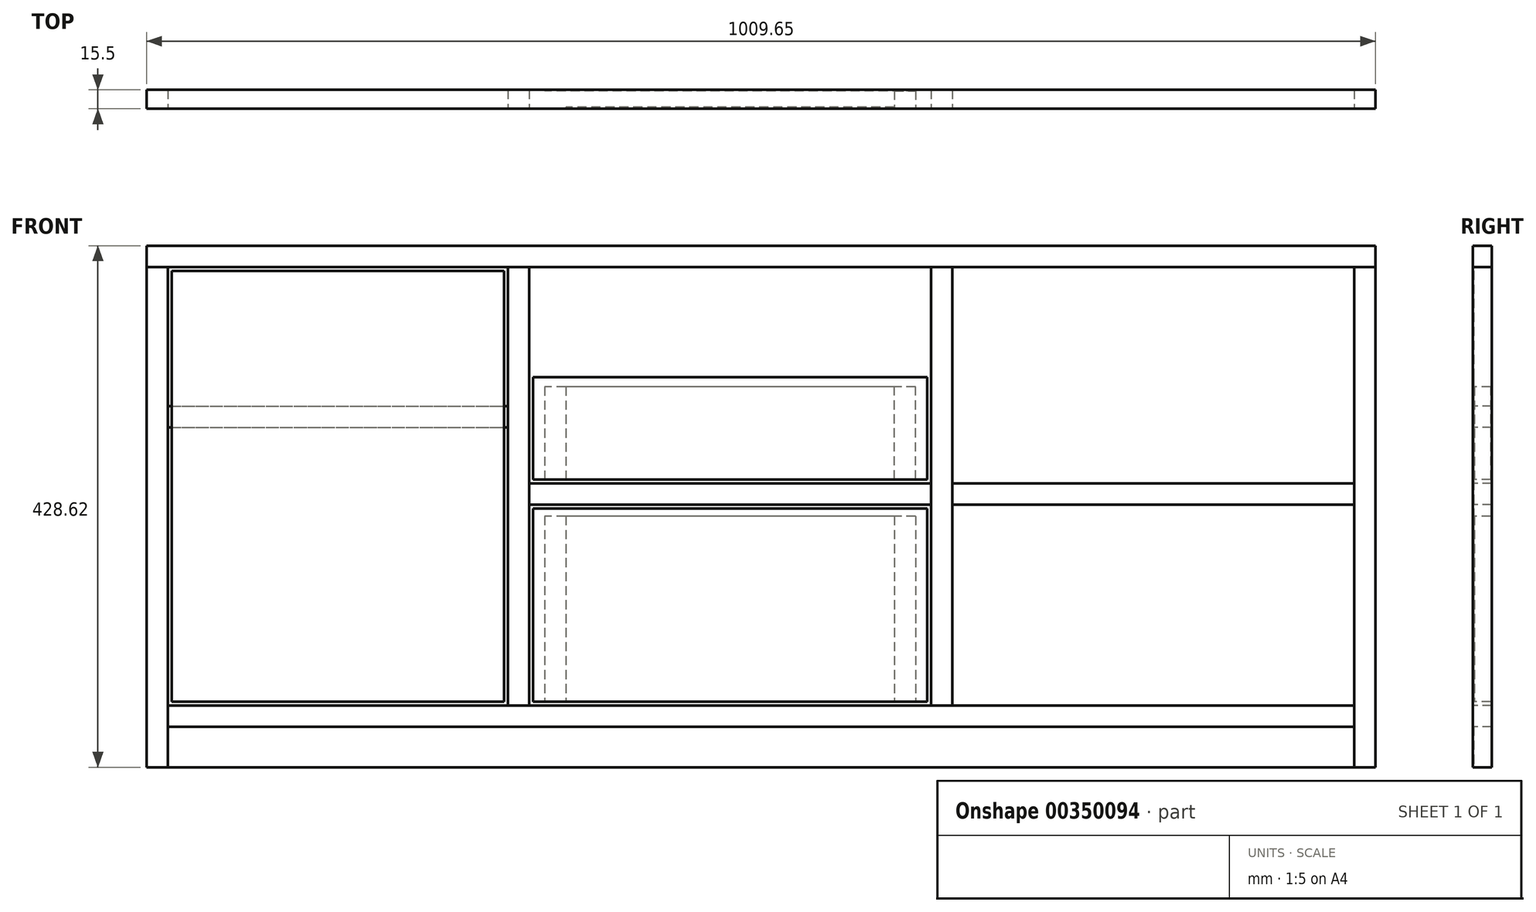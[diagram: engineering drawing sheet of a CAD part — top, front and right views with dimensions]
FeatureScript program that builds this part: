
annotation { "Feature Type Name" : "Feature", "Feature Type Description" : "" }
export const myFeature = defineFeature(function(context is Context, id is Id, definition is map)
    precondition{}
    {
        {
            assignVariable(context, id + "F0", {"name" : "Thk", "anyValue" : .6875});
        }
        {
            assignVariable(context, id + "F1", {"name" : "Depth", "anyValue" : 15.5});
        }
        {
            var Q0;
            Q0=qCreatedBy(makeId("Front.planeOp"),FACE);
            var sketch = newSketch(context, id + "F2", { "sketchPlane" : qUnion([Q0])});
            skLineSegment(sketch, "E0.bottom", {"start": v(0, 0) * mm, "end": v(1009.65, 0) * mm});
            skLineSegment(sketch, "E0.top", {"start": v(0, 428.62) * mm, "end": v(1009.65, 428.63) * mm});
            skLineSegment(sketch, "E0.left", {"start": v(0, 0) * mm, "end": v(0, 428.62) * mm});
            skLineSegment(sketch, "E0.right", {"start": v(1009.65, 0) * mm, "end": v(1009.65, 428.63) * mm});
            skLineSegment(sketch, "E1", {"start": v(17.46, 50.8) * mm, "end": v(992.19, 50.8) * mm});
            skLineSegment(sketch, "E2", {"start": v(17.46, 50.8) * mm, "end": v(17.46, 411.16) * mm});
            skLineSegment(sketch, "E3", {"start": v(17.46, 411.16) * mm, "end": v(992.19, 411.16) * mm});
            skLineSegment(sketch, "E4", {"start": v(992.19, 411.16) * mm, "end": v(992.19, 50.8) * mm});
            skLineSegment(sketch, "E5", {"start": v(314.33, 215.9) * mm, "end": v(314.32, 411.16) * mm});
            skLineSegment(sketch, "E6", {"start": v(314.33, 215.9) * mm, "end": v(314.33, 50.8) * mm});
            skLineSegment(sketch, "E7", {"start": v(17.46, 279.4) * mm, "end": v(296.86, 279.4) * mm});
            skLineSegment(sketch, "E8", {"start": v(296.86, 279.4) * mm, "end": v(296.86, 50.8) * mm});
            skLineSegment(sketch, "E9", {"start": v(17.46, 296.86) * mm, "end": v(296.86, 296.86) * mm});
            skLineSegment(sketch, "E10", {"start": v(296.86, 296.86) * mm, "end": v(296.86, 411.16) * mm});
            skLineSegment(sketch, "E11", {"start": v(314.32, 215.9) * mm, "end": v(644.52, 215.9) * mm});
            skLineSegment(sketch, "E12", {"start": v(314.32, 233.36) * mm, "end": v(644.52, 233.36) * mm});
            skLineSegment(sketch, "E13", {"start": v(653.26, 215.9) * mm, "end": v(653.26, 50.8) * mm, "construction": true});
            skLineSegment(sketch, "E14", {"start": v(661.99, 215.9) * mm, "end": v(661.99, 50.8) * mm});
            skLineSegment(sketch, "E15.MirrorCS", {"start": v(644.52, 215.9) * mm, "end": v(644.52, 50.8) * mm});
            skLineSegment(sketch, "E16", {"start": v(644.52, 233.36) * mm, "end": v(644.52, 411.16) * mm});
            skLineSegment(sketch, "E17", {"start": v(661.99, 233.36) * mm, "end": v(661.99, 411.16) * mm});
            skPoint(sketch, "E18.startSnap0", {"position": v(661.99, 322.26) * mm});
            skLineSegment(sketch, "E19", {"start": v(661.99, 322.26) * mm, "end": v(992.19, 322.26) * mm});
            skLineSegment(sketch, "E20", {"start": v(644.52, 322.26) * mm, "end": v(314.32, 322.26) * mm});
            skLineSegment(sketch, "E21", {"start": v(17.46, 411.16) * mm, "end": v(0, 411.16) * mm});
            skLineSegment(sketch, "E22", {"start": v(992.19, 411.16) * mm, "end": v(1009.65, 411.16) * mm});
            skLineSegment(sketch, "E23", {"start": v(17.46, 50.8) * mm, "end": v(17.46, 0) * mm});
            skLineSegment(sketch, "E24", {"start": v(17.46, 33.34) * mm, "end": v(992.19, 33.34) * mm});
            skLineSegment(sketch, "E25", {"start": v(992.19, 50.8) * mm, "end": v(992.19, 0) * mm});
            skLineSegment(sketch, "E26", {"start": v(296.86, 296.86) * mm, "end": v(296.86, 279.4) * mm});
            skLineSegment(sketch, "E27", {"start": v(644.52, 233.36) * mm, "end": v(644.52, 215.9) * mm});
            skLineSegment(sketch, "E28", {"start": v(661.99, 233.36) * mm, "end": v(661.99, 215.9) * mm});
            skLineSegment(sketch, "E29.trimOffspring", {"start": v(661.99, 233.36) * mm, "end": v(992.19, 233.36) * mm});
            skLineSegment(sketch, "E30.trimOffspring", {"start": v(661.99, 215.9) * mm, "end": v(992.19, 215.9) * mm});
            skSolve(sketch);
        }
        {
            var Q0;
            {var subQ4=sQuery(id+"F2.wireOp",EDGE,"E0.top");Q0=makeQuery(id+"F2.imprint","IMPRINT",FACE,{"disambiguationData":[TD([[makeQuery(id+"F2.imprint","IMPRINT",EDGE,{"derivedFrom":subQ4}),-1.0]])]});}
            extrude(context, id + "F3", {"entities" : qUnion([Q0]), "oppositeDirection" : true, "depth" : (getVariable(context, 'Depth')) * mm});
        }
        {
            var Q0;
            {var subQ10=sQuery(id+"F2.wireOp",EDGE,"E21");Q0=makeQuery(id+"F2.imprint","IMPRINT",FACE,{"disambiguationData":[TD([[makeQuery(id+"F2.imprint","IMPRINT",EDGE,{"derivedFrom":subQ10}),1.0]])]});}
            extrude(context, id + "F4", {"entities" : qUnion([Q0]), "oppositeDirection" : true, "depth" : (getVariable(context, 'Depth')) * mm});
        }
        {
            var Q0;
            {var subQ3=sQuery(id+"F2.wireOp",EDGE,"E6");Q0=makeQuery(id+"F2.imprint","IMPRINT",FACE,{"disambiguationData":[TD([[makeQuery(id+"F2.imprint","IMPRINT",EDGE,{"derivedFrom":subQ3}),-1.0]])]});}
            extrude(context, id + "F5", {"entities" : qUnion([Q0]), "oppositeDirection" : true, "depth" : (getVariable(context, 'Depth')) * mm});
        }
        {
            var Q0;
            {var subQ0=sQuery(id+"F2.wireOp",EDGE,"E14");Q0=makeQuery(id+"F2.imprint","IMPRINT",FACE,{"disambiguationData":[TD([[makeQuery(id+"F2.imprint","IMPRINT",EDGE,{"derivedFrom":subQ0}),-1.0]])]});}
            extrude(context, id + "F6", {"entities" : qUnion([Q0]), "oppositeDirection" : true, "depth" : (getVariable(context, 'Depth')) * mm});
        }
        {
            var Q0;
            {var subQ0=sQuery(id+"F2.wireOp",EDGE,"E22");Q0=makeQuery(id+"F2.imprint","IMPRINT",FACE,{"disambiguationData":[TD([[makeQuery(id+"F2.imprint","IMPRINT",EDGE,{"derivedFrom":subQ0}),-1.0]])]});}
            extrude(context, id + "F7", {"entities" : qUnion([Q0]), "oppositeDirection" : true, "depth" : (getVariable(context, 'Depth')) * mm});
        }
        {
            var Q0;
            {var subQ0=sQuery(id+"F2.wireOp",EDGE,"E7");Q0=makeQuery(id+"F2.imprint","IMPRINT",FACE,{"disambiguationData":[TD([[makeQuery(id+"F2.imprint","IMPRINT",EDGE,{"derivedFrom":subQ0}),1.0]])]});}
            extrude(context, id + "F8", {"entities" : qUnion([Q0]), "oppositeDirection" : true, "depth" : (getVariable(context, 'Depth')) * mm, "hasSecondDirection" : true, "secondDirectionOppositeDirection" : true, "secondDirectionDepth" : (getVariable(context, 'Thk')) * mm});
        }
        {
            var Q0;
            {var subQ9=sQuery(id+"F2.wireOp",EDGE,"E24");Q0=makeQuery(id+"F2.imprint","IMPRINT",FACE,{"disambiguationData":[TD([[makeQuery(id+"F2.imprint","IMPRINT",EDGE,{"derivedFrom":subQ9}),1.0]])]});}
            extrude(context, id + "F9", {"entities" : qUnion([Q0]), "oppositeDirection" : true, "depth" : (getVariable(context, 'Depth')) * mm});
        }
        {
            var Q0;
            {var subQ5=sQuery(id+"F2.wireOp",EDGE,"E24");Q0=makeQuery(id+"F2.imprint","IMPRINT",FACE,{"disambiguationData":[TD([[makeQuery(id+"F2.imprint","IMPRINT",EDGE,{"derivedFrom":subQ5}),-1.0]])]});}
            extrude(context, id + "F10", {"entities" : qUnion([Q0]), "oppositeDirection" : true, "depth" : (getVariable(context, 'Thk')) * mm});
        }
        {
            var Q0;
            {var subQ0=sQuery(id+"F2.wireOp",EDGE,"E11");Q0=makeQuery(id+"F2.imprint","IMPRINT",FACE,{"disambiguationData":[TD([[makeQuery(id+"F2.imprint","IMPRINT",EDGE,{"derivedFrom":subQ0}),1.0]])]});}
            extrude(context, id + "F11", {"entities" : qUnion([Q0]), "oppositeDirection" : true, "depth" : (getVariable(context, 'Depth')) * mm});
        }
        {
            var Q0;
            Q0=makeQuery(id+"F2.imprint","IMPRINT",FACE,{"disambiguationData":[TD([[makeQuery(id+"F2.imprint","IMPRINT",EDGE,{"derivedFrom":sQuery(id+"F2.wireOp",EDGE,"E28")}),1.0]])]});
            extrude(context, id + "F12", {"entities" : qUnion([Q0]), "oppositeDirection" : true, "depth" : (getVariable(context, 'Depth')) * mm});
        }
        {
            var Q0;
            Q0=qCreatedBy(makeId("Front.planeOp"),FACE);
            var sketch = newSketch(context, id + "F13", { "sketchPlane" : qUnion([Q0])});
            skLineSegment(sketch, "E31.bottom", {"start": v(317.5, 212.72) * mm, "end": v(641.35, 212.72) * mm});
            skLineSegment(sketch, "E31.top", {"start": v(317.5, 53.98) * mm, "end": v(641.35, 53.98) * mm});
            skLineSegment(sketch, "E31.left", {"start": v(317.5, 212.72) * mm, "end": v(317.5, 53.97) * mm});
            skLineSegment(sketch, "E31.right", {"start": v(641.35, 212.72) * mm, "end": v(641.35, 53.97) * mm});
            skSolve(sketch);
        }
        {
            var Q0;
            Q0 = qSketchRegion(id + "F13", true);
            extrude(context, id + "F14", {"entities" : qUnion([Q0]), "oppositeDirection" : true, "depth" : (getVariable(context, 'Thk')) * mm});
        }
        {
            var Q0;
            Q0=makeQuery(id+"F14.opExtrude","CAP_FACE",FACE,{"disambiguationData":[OSD([sQuery(id+"F13.wireOp",EDGE,"E31.bottom"),sQuery(id+"F13.wireOp",EDGE,"E31.top"),sQuery(id+"F13.wireOp",EDGE,"E31.left"),sQuery(id+"F13.wireOp",EDGE,"E31.right")])],"isStart":false});
            var sketch = newSketch(context, id + "F15", { "sketchPlane" : qUnion([Q0])});
            skLineSegment(sketch, "E32.bottom", {"start": v(-631.82, 206.37) * mm, "end": v(-614.36, 206.37) * mm});
            skLineSegment(sketch, "E32.top", {"start": v(-631.82, 53.98) * mm, "end": v(-614.36, 53.98) * mm});
            skLineSegment(sketch, "E32.left", {"start": v(-631.82, 206.37) * mm, "end": v(-631.82, 53.98) * mm});
            skLineSegment(sketch, "E32.right", {"start": v(-614.36, 206.37) * mm, "end": v(-614.36, 53.98) * mm});
            skSolve(sketch);
        }
        {
            var Q0;
            Q0=makeQuery(id+"F15.imprint","IMPRINT",FACE,{"disambiguationData":[TD([[makeQuery(id+"F15.imprint","IMPRINT",EDGE,{"derivedFrom":sQuery(id+"F15.wireOp",EDGE,"E32.bottom")}),-1.0]])]});
            extrude(context, id + "F16", {"entities" : qUnion([Q0]), "depth" : (getVariable(context, 'Depth') - 2 * getVariable(context, 'Thk')) * mm});
        }
        {
            var Q0;
            Q0=makeQuery(id+"F16.opExtrude","CAP_FACE",FACE,{"disambiguationData":[OSD([sQuery(id+"F15.wireOp",EDGE,"E32.bottom"),sQuery(id+"F15.wireOp",EDGE,"E32.top"),sQuery(id+"F15.wireOp",EDGE,"E32.left"),sQuery(id+"F15.wireOp",EDGE,"E32.right")])],"isStart":false});
            var sketch = newSketch(context, id + "F17", { "sketchPlane" : qUnion([Q0])});
            skLineSegment(sketch, "E33", {"start": v(-479.43, 53.97) * mm, "end": v(-479.43, 212.72) * mm, "construction": true});
            skLineSegment(sketch, "E34.bottom", {"start": v(-631.82, 206.37) * mm, "end": v(-327.03, 206.37) * mm});
            skLineSegment(sketch, "E34.top", {"start": v(-631.82, 53.98) * mm, "end": v(-327.03, 53.98) * mm});
            skLineSegment(sketch, "E34.left", {"start": v(-631.82, 206.37) * mm, "end": v(-631.82, 53.98) * mm});
            skLineSegment(sketch, "E34.right", {"start": v(-327.03, 206.37) * mm, "end": v(-327.03, 53.98) * mm});
            skSolve(sketch);
        }
        {
            var Q0;
            Q0 = qSketchRegion(id + "F17", true);
            extrude(context, id + "F18", {"entities" : qUnion([Q0]), "depth" : (getVariable(context, 'Thk')) * mm});
        }
        {
            var Q0;
            Q0=qCreatedBy(makeId("Front.planeOp"),FACE);
            var sketch = newSketch(context, id + "F19", { "sketchPlane" : qUnion([Q0])});
            skLineSegment(sketch, "E35.bottom", {"start": v(20.64, 407.99) * mm, "end": v(293.69, 407.99) * mm});
            skLineSegment(sketch, "E35.top", {"start": v(20.64, 53.97) * mm, "end": v(293.69, 53.97) * mm});
            skLineSegment(sketch, "E35.left", {"start": v(20.64, 407.99) * mm, "end": v(20.64, 53.97) * mm});
            skLineSegment(sketch, "E35.right", {"start": v(293.69, 407.99) * mm, "end": v(293.69, 53.97) * mm});
            skSolve(sketch);
        }
        {
            var Q0;
            Q0 = qSketchRegion(id + "F19", true);
            extrude(context, id + "F20", {"entities" : qUnion([Q0]), "oppositeDirection" : true, "depth" : (getVariable(context, 'Thk')) * mm});
        }
        {
            var Q0;
            Q0=qCreatedBy(makeId("Front.planeOp"),FACE);
            var sketch = newSketch(context, id + "F21", { "sketchPlane" : qUnion([Q0])});
            skLineSegment(sketch, "E36.bottom", {"start": v(317.5, 320.67) * mm, "end": v(641.35, 320.68) * mm});
            skLineSegment(sketch, "E36.top", {"start": v(317.5, 236.54) * mm, "end": v(641.35, 236.54) * mm});
            skLineSegment(sketch, "E36.left", {"start": v(317.5, 320.67) * mm, "end": v(317.5, 236.54) * mm});
            skLineSegment(sketch, "E36.right", {"start": v(641.35, 320.68) * mm, "end": v(641.35, 236.54) * mm});
            skSolve(sketch);
        }
        {
            var Q0;
            Q0 = qSketchRegion(id + "F21", true);
            extrude(context, id + "F22", {"entities" : qUnion([Q0]), "oppositeDirection" : true, "depth" : (getVariable(context, 'Thk')) * mm});
        }
        {
            var Q0;
            Q0=makeQuery(id+"F14.opExtrude","CAP_FACE",FACE,{"disambiguationData":[OSD([sQuery(id+"F13.wireOp",EDGE,"E31.bottom"),sQuery(id+"F13.wireOp",EDGE,"E31.top"),sQuery(id+"F13.wireOp",EDGE,"E31.left"),sQuery(id+"F13.wireOp",EDGE,"E31.right")])],"isStart":false});
            var sketch = newSketch(context, id + "F23", { "sketchPlane" : qUnion([Q0])});
            skLineSegment(sketch, "E37.bottom", {"start": v(-614.36, 206.37) * mm, "end": v(-344.49, 206.37) * mm});
            skLineSegment(sketch, "E37.top", {"start": v(-614.36, 53.98) * mm, "end": v(-344.49, 53.98) * mm});
            skLineSegment(sketch, "E37.left", {"start": v(-614.36, 206.37) * mm, "end": v(-614.36, 53.97) * mm});
            skLineSegment(sketch, "E37.right", {"start": v(-344.49, 206.38) * mm, "end": v(-344.49, 53.98) * mm});
            skPoint(sketch, "E38", {"position": v(-479.43, 53.98) * mm});
            skSolve(sketch);
        }
        {
            var Q0;
            Q0 = qSketchRegion(id + "F23", true);
            extrude(context, id + "F24", {"entities" : qUnion([Q0]), "depth" : (getVariable(context, 'Thk')) * mm});
        }
        {
            var Q0;
            Q0=makeQuery(id+"F22.opExtrude","CAP_FACE",FACE,{"disambiguationData":[OSD([sQuery(id+"F21.wireOp",EDGE,"E36.bottom"),sQuery(id+"F21.wireOp",EDGE,"E36.top"),sQuery(id+"F21.wireOp",EDGE,"E36.left"),sQuery(id+"F21.wireOp",EDGE,"E36.right")])],"isStart":false});
            var sketch = newSketch(context, id + "F25", { "sketchPlane" : qUnion([Q0])});
            skLineSegment(sketch, "E39.bottom", {"start": v(-631.82, 236.54) * mm, "end": v(-614.36, 236.54) * mm});
            skLineSegment(sketch, "E39.top", {"start": v(-631.82, 312.74) * mm, "end": v(-614.36, 312.74) * mm});
            skLineSegment(sketch, "E39.left", {"start": v(-631.82, 236.54) * mm, "end": v(-631.82, 312.74) * mm});
            skLineSegment(sketch, "E39.right", {"start": v(-614.36, 236.54) * mm, "end": v(-614.36, 312.74) * mm});
            skSolve(sketch);
        }
        {
            var Q0;
            Q0 = qSketchRegion(id + "F25", true);
            extrude(context, id + "F26", {"entities" : qUnion([Q0]), "depth" : (getVariable(context, 'Depth') - 2 * getVariable(context, 'Thk')) * mm});
        }
        {
            var Q0;
            Q0=makeQuery(id+"F22.opExtrude","CAP_FACE",FACE,{"disambiguationData":[OSD([sQuery(id+"F21.wireOp",EDGE,"E36.bottom"),sQuery(id+"F21.wireOp",EDGE,"E36.top"),sQuery(id+"F21.wireOp",EDGE,"E36.left"),sQuery(id+"F21.wireOp",EDGE,"E36.right")])],"isStart":false});
            var sketch = newSketch(context, id + "F27", { "sketchPlane" : qUnion([Q0])});
            skLineSegment(sketch, "E40.bottom", {"start": v(-614.36, 312.74) * mm, "end": v(-344.49, 312.74) * mm});
            skLineSegment(sketch, "E40.top", {"start": v(-614.36, 236.54) * mm, "end": v(-344.49, 236.54) * mm});
            skLineSegment(sketch, "E40.left", {"start": v(-614.36, 312.74) * mm, "end": v(-614.36, 236.54) * mm});
            skLineSegment(sketch, "E40.right", {"start": v(-344.49, 312.74) * mm, "end": v(-344.49, 236.54) * mm});
            skPoint(sketch, "E41", {"position": v(-479.43, 236.54) * mm});
            skSolve(sketch);
        }
        {
            var Q0;
            Q0 = qSketchRegion(id + "F27", true);
            extrude(context, id + "F28", {"entities" : qUnion([Q0]), "depth" : (getVariable(context, 'Thk')) * mm});
        }
        {
            var Q0;
            Q0=makeQuery(id+"F26.opExtrude","CAP_FACE",FACE,{"disambiguationData":[OSD([sQuery(id+"F25.wireOp",EDGE,"E39.bottom"),sQuery(id+"F25.wireOp",EDGE,"E39.top"),sQuery(id+"F25.wireOp",EDGE,"E39.left"),sQuery(id+"F25.wireOp",EDGE,"E39.right")])],"isStart":false});
            var sketch = newSketch(context, id + "F29", { "sketchPlane" : qUnion([Q0])});
            skLineSegment(sketch, "E42.bottom", {"start": v(-631.82, 312.74) * mm, "end": v(-327.03, 312.74) * mm});
            skLineSegment(sketch, "E42.top", {"start": v(-631.82, 236.54) * mm, "end": v(-327.03, 236.54) * mm});
            skLineSegment(sketch, "E42.left", {"start": v(-631.82, 312.74) * mm, "end": v(-631.82, 236.54) * mm});
            skLineSegment(sketch, "E42.right", {"start": v(-327.03, 312.74) * mm, "end": v(-327.03, 236.54) * mm});
            skPoint(sketch, "E43", {"position": v(-479.43, 236.54) * mm});
            skSolve(sketch);
        }
        {
            var Q0;
            Q0 = qSketchRegion(id + "F29", true);
            extrude(context, id + "F30", {"entities" : qUnion([Q0]), "depth" : (getVariable(context, 'Thk')) * mm});
        }
    });
